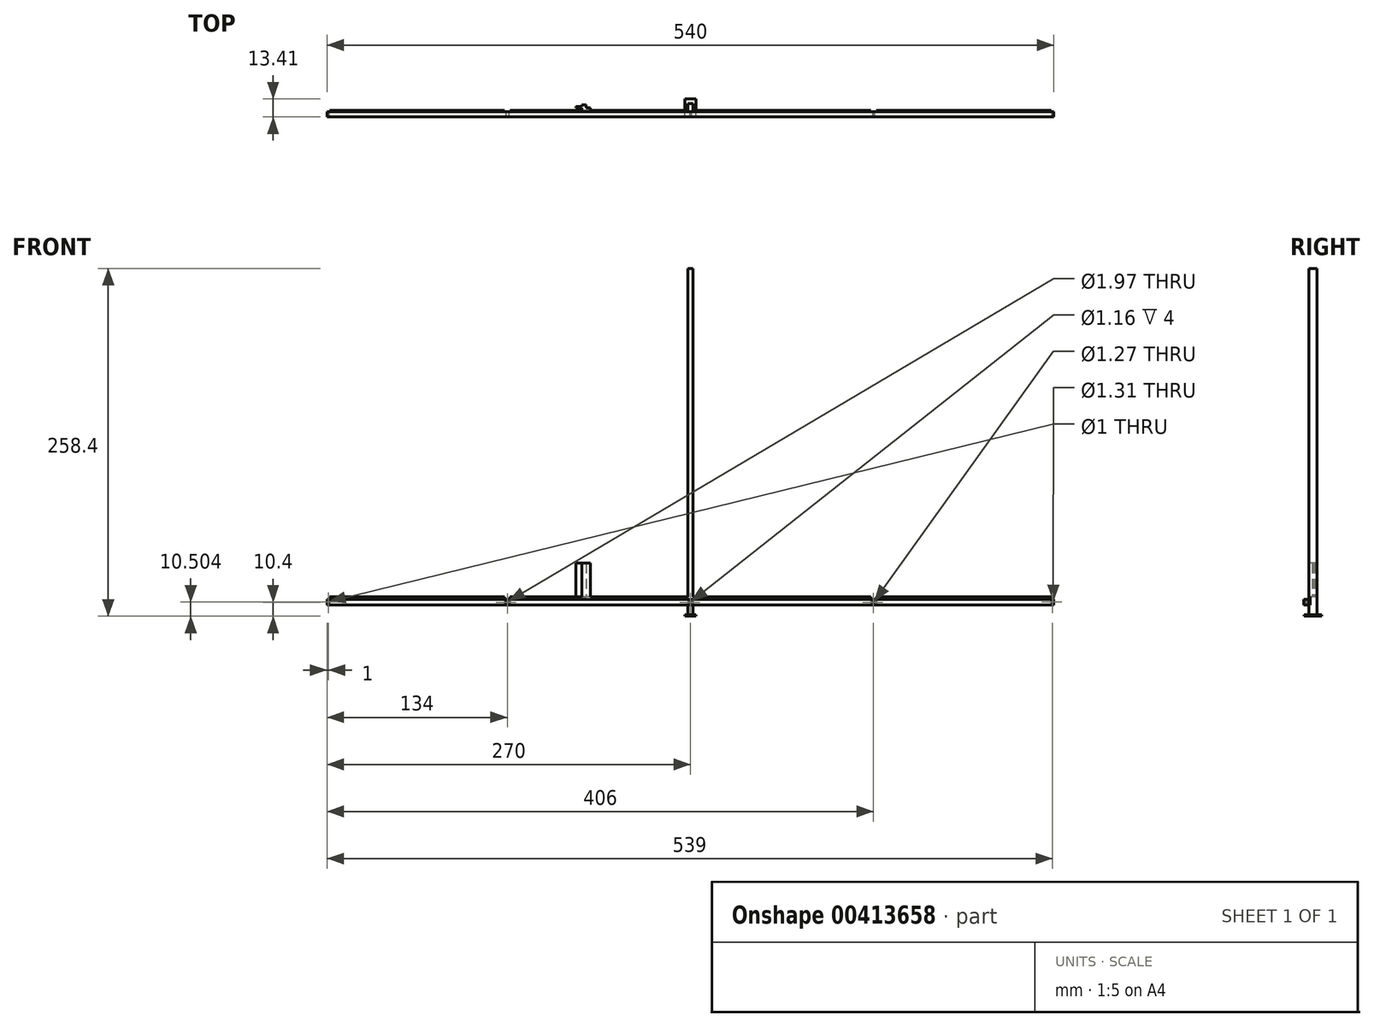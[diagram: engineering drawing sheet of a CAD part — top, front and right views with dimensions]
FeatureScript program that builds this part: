
annotation { "Feature Type Name" : "Feature", "Feature Type Description" : "" }
export const myFeature = defineFeature(function(context is Context, id is Id, definition is map)
    precondition{}
    {
        {
            var Q0;
            Q0=qCreatedBy(makeId("Top.planeOp"),FACE);
            var sketch = newSketch(context, id + "F0", { "sketchPlane" : qUnion([Q0])});
            skLineSegment(sketch, "E0", {"start": v(-270, 0) * mm, "end": v(-270, -4) * mm});
            skLineSegment(sketch, "E1", {"start": v(-270, -4) * mm, "end": v(270, -4) * mm});
            skLineSegment(sketch, "E2", {"start": v(270, -4) * mm, "end": v(270, 0) * mm});
            skLineSegment(sketch, "E3", {"start": v(270, 0) * mm, "end": v(268, 0) * mm});
            skLineSegment(sketch, "E4", {"start": v(268, 0) * mm, "end": v(268, 1) * mm});
            skLineSegment(sketch, "E5", {"start": v(268, 1) * mm, "end": v(138, 1) * mm});
            skLineSegment(sketch, "E6", {"start": v(138, 1) * mm, "end": v(138, 0) * mm});
            skLineSegment(sketch, "E7", {"start": v(138, 0) * mm, "end": v(134, 0) * mm});
            skLineSegment(sketch, "E8", {"start": v(134, 0) * mm, "end": v(134, 1) * mm});
            skLineSegment(sketch, "E9", {"start": v(134, 1) * mm, "end": v(2, 1) * mm});
            skLineSegment(sketch, "E10", {"start": v(2, 1) * mm, "end": v(2, 0) * mm});
            skLineSegment(sketch, "E11", {"start": v(2, 0) * mm, "end": v(-2, 0) * mm});
            skLineSegment(sketch, "E12", {"start": v(-2, 0) * mm, "end": v(-2, 1) * mm});
            skLineSegment(sketch, "E13", {"start": v(-2, 1) * mm, "end": v(-134, 1) * mm});
            skLineSegment(sketch, "E14", {"start": v(-134, 1) * mm, "end": v(-134, 0) * mm});
            skLineSegment(sketch, "E15", {"start": v(-134, 0) * mm, "end": v(-138, 0) * mm});
            skLineSegment(sketch, "E16", {"start": v(-138, 0) * mm, "end": v(-138, 1) * mm});
            skLineSegment(sketch, "E17", {"start": v(-138, 1) * mm, "end": v(-268, 1) * mm});
            skLineSegment(sketch, "E18", {"start": v(-268, 1) * mm, "end": v(-268, 0) * mm});
            skLineSegment(sketch, "E19", {"start": v(-268, 0) * mm, "end": v(-270, 0) * mm});
            skSolve(sketch);
        }
        {
            var Q0;
            Q0 = qSketchRegion(id + "F0", true);
            extrude(context, id + "F1", {"entities" : qUnion([Q0]), "depth" : 4 * mm});
        }
        {
            var Q0;
            Q0=makeQuery(id+"F1.opExtrude","CAP_FACE",FACE,{"disambiguationData":[OSD([sQuery(id+"F0.wireOp",EDGE,"E0"),sQuery(id+"F0.wireOp",EDGE,"E1"),sQuery(id+"F0.wireOp",EDGE,"E2"),sQuery(id+"F0.wireOp",EDGE,"E3"),sQuery(id+"F0.wireOp",EDGE,"E4"),sQuery(id+"F0.wireOp",EDGE,"E5"),sQuery(id+"F0.wireOp",EDGE,"E6"),sQuery(id+"F0.wireOp",EDGE,"E7"),sQuery(id+"F0.wireOp",EDGE,"E8"),sQuery(id+"F0.wireOp",EDGE,"E9"),sQuery(id+"F0.wireOp",EDGE,"E10"),sQuery(id+"F0.wireOp",EDGE,"E11"),sQuery(id+"F0.wireOp",EDGE,"E12"),sQuery(id+"F0.wireOp",EDGE,"E13"),sQuery(id+"F0.wireOp",EDGE,"E14"),sQuery(id+"F0.wireOp",EDGE,"E15"),sQuery(id+"F0.wireOp",EDGE,"E16"),sQuery(id+"F0.wireOp",EDGE,"E17"),sQuery(id+"F0.wireOp",EDGE,"E18"),sQuery(id+"F0.wireOp",EDGE,"E19")])],"isStart":false});
            var sketch = newSketch(context, id + "F2", { "sketchPlane" : qUnion([Q0])});
            skLineSegment(sketch, "E20.bottom", {"start": v(-268, 1) * mm, "end": v(-138, 1) * mm});
            skLineSegment(sketch, "E20.top", {"start": v(-268, 0) * mm, "end": v(-138, 0) * mm});
            skLineSegment(sketch, "E20.left", {"start": v(-268, 1) * mm, "end": v(-268, 0) * mm});
            skLineSegment(sketch, "E20.right", {"start": v(-138, 1) * mm, "end": v(-138, 0) * mm});
            skLineSegment(sketch, "E21.bottom", {"start": v(-134, 1) * mm, "end": v(-2, 1) * mm});
            skLineSegment(sketch, "E21.top", {"start": v(-134, 0) * mm, "end": v(-2, 0) * mm});
            skLineSegment(sketch, "E21.left", {"start": v(-134, 1) * mm, "end": v(-134, 0) * mm});
            skLineSegment(sketch, "E21.right", {"start": v(-2, 1) * mm, "end": v(-2, 0) * mm});
            skLineSegment(sketch, "E22.bottom", {"start": v(2, 1) * mm, "end": v(134, 1) * mm});
            skLineSegment(sketch, "E22.top", {"start": v(2, 0) * mm, "end": v(134, 0) * mm});
            skLineSegment(sketch, "E22.left", {"start": v(2, 1) * mm, "end": v(2, 0) * mm});
            skLineSegment(sketch, "E22.right", {"start": v(134, 1) * mm, "end": v(134, 0) * mm});
            skLineSegment(sketch, "E23.bottom", {"start": v(268, 1) * mm, "end": v(138, 1) * mm});
            skLineSegment(sketch, "E23.top", {"start": v(268, 0) * mm, "end": v(138, 0) * mm});
            skLineSegment(sketch, "E23.left", {"start": v(268, 1) * mm, "end": v(268, 0) * mm});
            skLineSegment(sketch, "E23.right", {"start": v(138, 1) * mm, "end": v(138, 0) * mm});
            skSolve(sketch);
        }
        {
            var Q0;
            Q0 = qSketchRegion(id + "F2", true);
            extrude(context, id + "F3", {"entities" : qUnion([Q0]), "operationType" : NewBodyOperationType.ADD, "depth" : 2 * mm});
        }
        {
            var Q0;
            Q0=makeQuery(id+"F1.opExtrude","SWEPT_FACE",FACE,{"disambiguationData":[OSD([sQuery(id+"F0.wireOp",EDGE,"E1")])]});
            var sketch = newSketch(context, id + "F4", { "sketchPlane" : qUnion([Q0])});
            skCircle(sketch, "E24", {"center": v(-269, 2.1) * mm, "radius": 0.5 * mm});
            skCircle(sketch, "E25", {"center": v(-136, 2) * mm, "radius": 0.99 * mm});
            skCircle(sketch, "E26", {"center": v(0, 2) * mm, "radius": 0.58 * mm});
            skCircle(sketch, "E27", {"center": v(269, 2.1) * mm, "radius": 0.65 * mm});
            skCircle(sketch, "E28", {"center": v(136, 2) * mm, "radius": 0.64 * mm});
            skSolve(sketch);
        }
        {
            var Q0;
            Q0 = qSketchRegion(id + "F4", true);
            extrude(context, id + "F5", {"entities" : qUnion([Q0]), "operationType" : NewBodyOperationType.REMOVE, "oppositeDirection" : true, "depth" : 6.3 * mm});
        }
        {
            var Q0;
            Q0=qCreatedBy(makeId("Top.planeOp"),FACE);
            var sketch = newSketch(context, id + "F6", { "sketchPlane" : qUnion([Q0])});
            skLineSegment(sketch, "E29.bottom", {"start": v(-2, 6) * mm, "end": v(2, 6) * mm});
            skLineSegment(sketch, "E29.top", {"start": v(-2, 0) * mm, "end": v(2, 0) * mm});
            skLineSegment(sketch, "E29.left", {"start": v(-2, 6) * mm, "end": v(-2, 0) * mm});
            skLineSegment(sketch, "E29.right", {"start": v(2, 6) * mm, "end": v(2, 0) * mm});
            skSolve(sketch);
        }
        {
            var Q0;
            Q0 = qSketchRegion(id + "F6", true);
            extrude(context, id + "F7", {"entities" : qUnion([Q0]), "depth" : 250 * mm});
        }
        {
            var Q0;
            Q0 = qSketchRegion(id + "F6", true);
            extrude(context, id + "F8", {"entities" : qUnion([Q0]), "operationType" : NewBodyOperationType.ADD, "oppositeDirection" : true, "depth" : 7.4 * mm});
        }
        {
            var Q0;
            Q0=makeQuery(id+"F8.opExtrude","CAP_FACE",FACE,{"disambiguationData":[OSD([sQuery(id+"F6.wireOp",EDGE,"E29.bottom"),sQuery(id+"F6.wireOp",EDGE,"E29.top"),sQuery(id+"F6.wireOp",EDGE,"E29.left"),sQuery(id+"F6.wireOp",EDGE,"E29.right")])],"isStart":false});
            var sketch = newSketch(context, id + "F9", { "sketchPlane" : qUnion([Q0])});
            skLineSegment(sketch, "E30.bottom", {"start": v(-4.03, 3.65) * mm, "end": v(4.03, 3.65) * mm});
            skLineSegment(sketch, "E30.top", {"start": v(-4.03, -9.4) * mm, "end": v(4.03, -9.4) * mm});
            skLineSegment(sketch, "E30.left", {"start": v(-4.03, 3.65) * mm, "end": v(-4.03, -9.4) * mm});
            skLineSegment(sketch, "E30.right", {"start": v(4.03, 3.65) * mm, "end": v(4.03, -9.4) * mm});
            skSolve(sketch);
        }
        {
            var Q0;
            Q0=makeQuery(id+"F9.imprint","IMPRINT",FACE,{"disambiguationData":[TD([[makeQuery(id+"F9.imprint","IMPRINT",EDGE,{"derivedFrom":sQuery(id+"F9.wireOp",EDGE,"E30.bottom")}),-1.0]])]});
            var Q1;
            Q1=makeQuery(id+"F9.imprint","IMPRINT",FACE,{"disambiguationData":[TD([[makeQuery(id+"F9.imprint","IMPRINT",EDGE,{"derivedFrom":makeQuery(id+"F8.opExtrude","CAP_EDGE",EDGE,{"disambiguationData":[OSD([sQuery(id+"F6.wireOp",EDGE,"E29.bottom")])],"isStart":false})}),1.0]])]});
            extrude(context, id + "F10", {"entities" : qUnion([Q0, Q1]), "depth" : 1 * mm});
        }
        {
            var Q0;
            Q0=makeQuery(id+"F3.opExtrude","CAP_FACE",FACE,{"disambiguationData":[OSD([sQuery(id+"F2.wireOp",EDGE,"E21.bottom"),sQuery(id+"F2.wireOp",EDGE,"E21.top"),sQuery(id+"F2.wireOp",EDGE,"E21.left"),sQuery(id+"F2.wireOp",EDGE,"E21.right")])],"isStart":false});
            var sketch = newSketch(context, id + "F11", { "sketchPlane" : qUnion([Q0])});
            skLineSegment(sketch, "E31.bottom", {"start": v(-74.38, 2.6) * mm, "end": v(-80.65, 2.6) * mm});
            skLineSegment(sketch, "E31.top", {"start": v(-74.38, 0) * mm, "end": v(-80.65, 0) * mm});
            skLineSegment(sketch, "E31.left", {"start": v(-74.38, 2.6) * mm, "end": v(-74.38, 0) * mm});
            skLineSegment(sketch, "E31.right", {"start": v(-80.65, 2.6) * mm, "end": v(-80.65, 0) * mm});
            skPoint(sketch, "E32.oppositeSnap0", {"position": v(-77.51, 2.6) * mm});
            skLineSegment(sketch, "E32.bottom", {"start": v(-80.65, 5.05) * mm, "end": v(-77.51, 5.05) * mm});
            skLineSegment(sketch, "E32.top", {"start": v(-80.65, 1) * mm, "end": v(-77.51, 1) * mm});
            skLineSegment(sketch, "E32.left", {"start": v(-80.65, 5.05) * mm, "end": v(-80.65, 1) * mm});
            skLineSegment(sketch, "E32.right", {"start": v(-77.51, 5.05) * mm, "end": v(-77.51, 1) * mm});
            skLineSegment(sketch, "E33.bottom", {"start": v(-84.97, 3.7) * mm, "end": v(-80.65, 3.7) * mm});
            skLineSegment(sketch, "E33.top", {"start": v(-84.97, 2.6) * mm, "end": v(-80.65, 2.6) * mm});
            skLineSegment(sketch, "E33.left", {"start": v(-84.97, 3.7) * mm, "end": v(-84.97, 2.6) * mm});
            skLineSegment(sketch, "E33.right", {"start": v(-80.65, 3.7) * mm, "end": v(-80.65, 2.6) * mm});
            skSolve(sketch);
        }
        {
            var Q0;
            Q0 = qSketchRegion(id + "F11", true);
            extrude(context, id + "F12", {"entities" : qUnion([Q0]), "operationType" : NewBodyOperationType.ADD, "depth" : 25 * mm});
        }
    });
